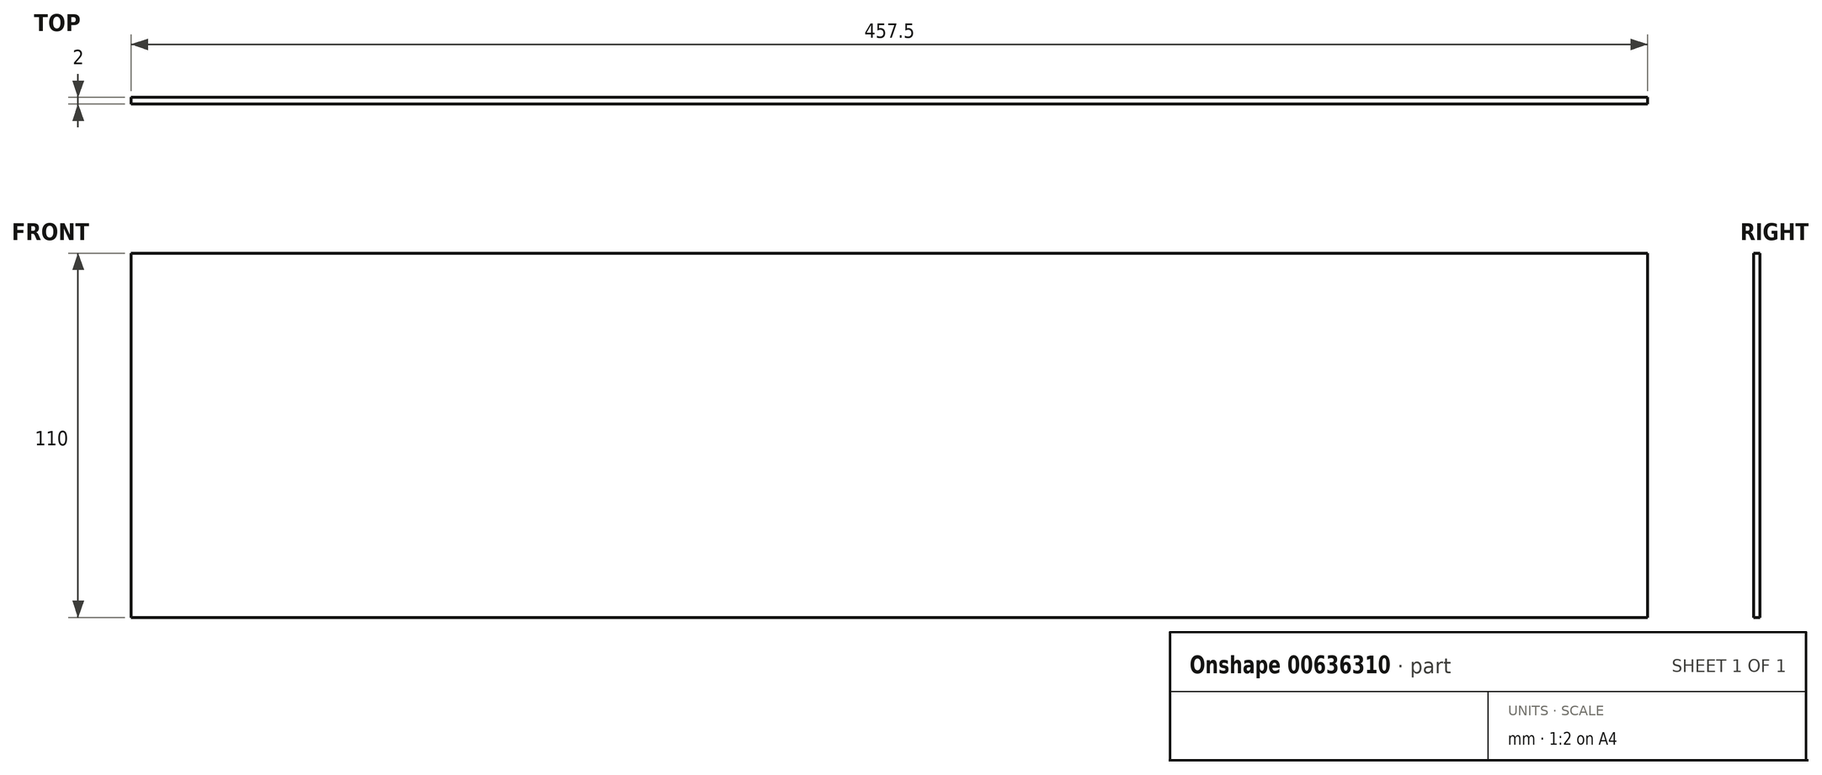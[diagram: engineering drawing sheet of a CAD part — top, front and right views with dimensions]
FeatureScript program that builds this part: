
annotation { "Feature Type Name" : "Feature", "Feature Type Description" : "" }
export const myFeature = defineFeature(function(context is Context, id is Id, definition is map)
    precondition{}
    {
        {
            var Q0;
            Q0=qCreatedBy(makeId("Front.planeOp"),FACE);
            var sketch = newSketch(context, id + "F0", { "sketchPlane" : qUnion([Q0])});
            skLineSegment(sketch, "E0.bottom", {"start": v(0, 0) * mm, "end": v(457.5, 0) * mm});
            skLineSegment(sketch, "E0.top", {"start": v(0, 110) * mm, "end": v(457.5, 110) * mm});
            skLineSegment(sketch, "E0.left", {"start": v(0, 0) * mm, "end": v(0, 110) * mm});
            skLineSegment(sketch, "E0.right", {"start": v(457.5, 0) * mm, "end": v(457.5, 110) * mm});
            skSolve(sketch);
        }
        {
            var Q0;
            Q0=qSketchRegion(id+"F0",true);
            extrude(context, id + "F1", {"entities" : qUnion([Q0]), "depth" : 2 * mm, "offsetDistance" : 25 * mm});
        }
    });
